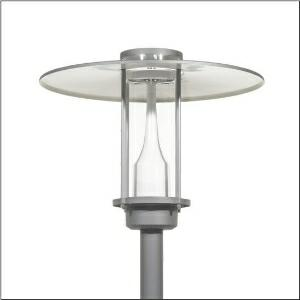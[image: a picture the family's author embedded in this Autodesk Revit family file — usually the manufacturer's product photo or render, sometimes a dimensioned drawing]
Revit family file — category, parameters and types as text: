
# Revit family: city-light_plus_iq___p1_0a_5xa5275ff14h000022_8535
name_source: partatom
category: Lighting Fixtures
units: mm (PartAtom-declared; Revit-internal decimal feet)

## family parameters
Cut with Voids When Loaded = No
Host = Face
Light Source = No
Part Type = Normal
Room Calculation Point = No
Round Connector Dimension = Use Diameter
Shared = No

## types (1)
- --- (1 x LED, 1440 lm, 10.5 W, 3000K)
    Apparent Load = 11 VA
    CIE Flux Codes = 32 61 90 96 100
    Color Rendering = 70
    Color Temperature = 3000K
    Default Elevation = 1800 mm
    Description = City-Light Plus iQ, mast luminaire, Module 540 iQ-SR, primary light control with 3 zone facetted reflector, of plastic, silver coated, highly specular, structured, primary optical cover: cover, of PMMA, transparent, light distribution: P1.0a, light emission: direct distribution, primary light characteristic: strongly asymmetric, installation type: post-top, LED, High Power LED, rated luminous flux: 1.440lm, luminous efficacy: 137lm/W, light colour: 730, colour temperature: 3000K, control gear: iQ Street-Remote, control: Street-Remote, Auto-Match, Temp-Guard, Lumen-Switch, Night-Set, Smart-Wire, Light-Fading, Desk-Remote (wireless, voltage-free reading and setting of iQ features in the workshop via application-optimized NFC function/RFID function), optimised constant luminous flux control (CLO 2.0), pre-setting: logarithmic dimming characteristic, mains connection: 230..240V, AC, 50/60Hz, connection cable pre-assembled, cable length: 5,5m, wiring characteristics: H07RN-F, start of lifetime: 11W, end of service life: 11W, reduction: 5W, luminaire housing, upper part, of glass-fibre reinforced polyester, coated, Siteco® metallic grey (DB 702S), diameter: 750mm, height: 590mm, spigot size: d x l = 76 x 70mm (post-top) | with reducer (optional accessory) 60 x 70mm, mounting height: 3..5m, post-top mast mounting element, of diecast aluminium, coated, Siteco® metallic grey (DB 702S), Module 540 iQ-SR, traffic white (RAL 9016), equipment: standard, protection rating (complete): IP65, insulation class (complete): insulation class II (safety insulation), certification: CE, ENEC, VDE, packaging unit: 1 piece

Light Distribution: P1.0a
    Height = 590 mm
    Lamp = 1 x LED
    Lamp Light Flux = 1440 lm
    Lamp Power = 10.5 W
    Lamp count = 1
    Length = 750 mm
    Luminous efficacy = 137 lm/W
    Manufacturer = Siteco
    ModVariant = No
    Model = 5XA5275FF14H000022
    Number of Poles = 1
    OnlyDefault = Yes
    Power Factor = 1
    Product Name = City-Light Plus iQ | P1.0a
    Product group = mast luminaire | pylon top
    ProductGroupID = 6100
    Protection Class = Protection class II
    Protection Degree = IP 65
    RLX_Detail_Level = 1
    RLX_Emergency_Light_Flux = 0 lm
    RLX_Emergency_Type = 0
    RLX_Emergency_Type_DB = No
    RlxData = <blob elided: 34257 chars, md5=02221c3e>
    Socket = socket
    Standby Power = 0 W
    System Light Flux = 1440 lm
    System Power = 11 W
    Type Comments = factory setting: luminous flux: 100 % | dim-lin: 254 | 419 mA
    Type Image = l_1006456.jpg
    URL = http://relux.com
    VarID = @adj_159946
    Voltage = 0 V
    Weight = 0.00 kg
    Width = 0 mm  [stored 0 ft]

note: [stored X ft] marks values corroborated as IEEE doubles in the binary element streams (Revit-internal decimal feet)

## geometry (parser evidence)
native form markers: Blend x4, Sweep x11
no freeform markers — native parametric forms only
